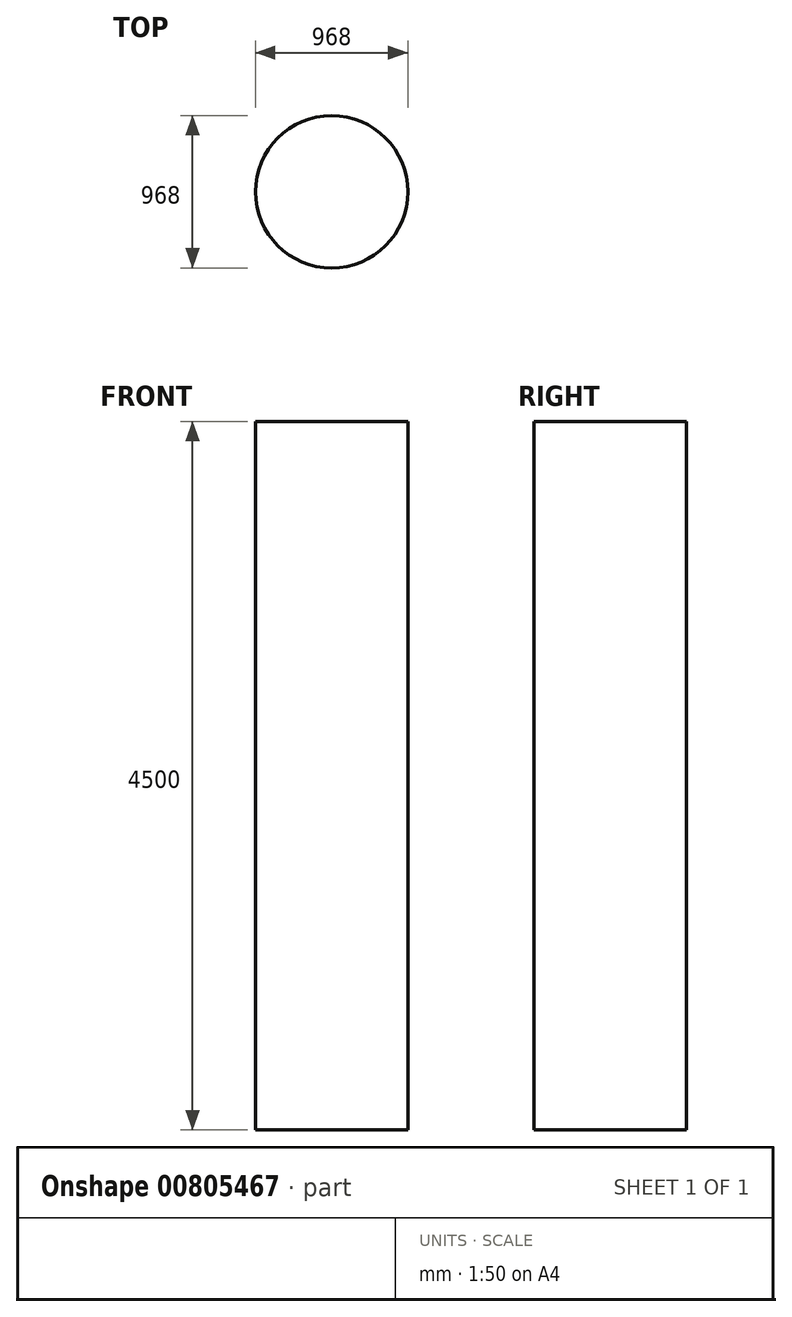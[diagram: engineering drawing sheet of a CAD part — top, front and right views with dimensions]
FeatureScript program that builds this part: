
annotation { "Feature Type Name" : "Feature", "Feature Type Description" : "" }
export const myFeature = defineFeature(function(context is Context, id is Id, definition is map)
    precondition{}
    {
        {
            var Q0;
            Q0=qCreatedBy(makeId("Top.planeOp"),FACE);
            var sketch = newSketch(context, id + "F0", { "sketchPlane" : qUnion([Q0])});
            skCircle(sketch, "E0", {"center": v(0, 0) * mm, "radius": 484 * mm});
            skSolve(sketch);
        }
        {
            var Q0;
            Q0 = qSketchRegion(id + "F0", true);
            extrude(context, id + "F1", {"entities" : qUnion([Q0]), "oppositeDirection" : true, "depth" : 4500 * mm, "offsetDistance" : 25 * mm});
        }
    });
